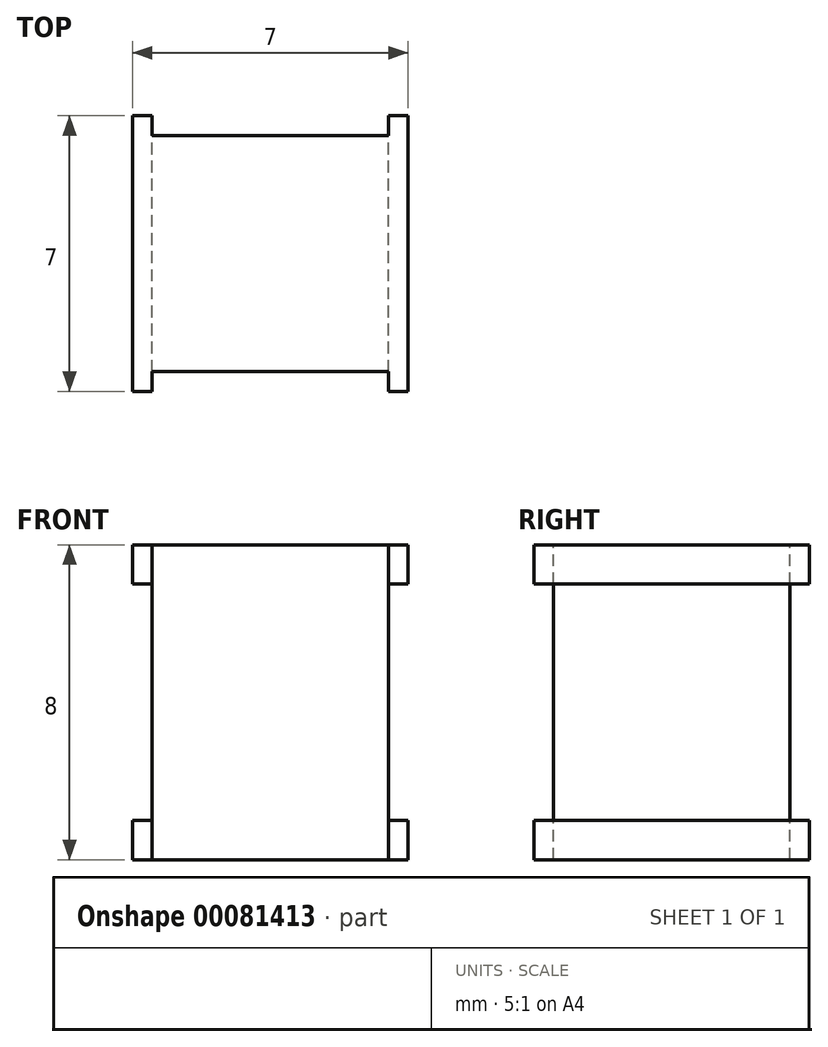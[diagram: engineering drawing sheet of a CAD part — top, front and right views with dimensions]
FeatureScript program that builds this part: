
annotation { "Feature Type Name" : "Feature", "Feature Type Description" : "" }
export const myFeature = defineFeature(function(context is Context, id is Id, definition is map)
    precondition{}
    {
        {
            var Q0;
            Q0=qCreatedBy(makeId("Top.planeOp"),FACE);
            var sketch = newSketch(context, id + "F0", { "sketchPlane" : qUnion([Q0])});
            skLineSegment(sketch, "E0.bottom", {"start": v(3, -3) * mm, "end": v(-3, -3) * mm});
            skLineSegment(sketch, "E0.top", {"start": v(3, 3) * mm, "end": v(-3, 3) * mm});
            skLineSegment(sketch, "E0.left", {"start": v(3, -3) * mm, "end": v(3, 3) * mm});
            skLineSegment(sketch, "E0.right", {"start": v(-3, -3) * mm, "end": v(-3, 3) * mm});
            skPoint(sketch, "E0.middle", {"position": v(0, 0) * mm});
            skSolve(sketch);
        }
        {
            var Q0;
            Q0=makeQuery(id+"F0.imprint","IMPRINT",FACE,{"disambiguationData":[TD([[makeQuery(id+"F0.imprint","IMPRINT",EDGE,{"derivedFrom":sQuery(id+"F0.wireOp",EDGE,"E0.bottom")}),-1.0]])]});
            extrude(context, id + "F1", {"entities" : qUnion([Q0]), "depth" : 6 * mm});
        }
        {
            var Q0;
            Q0=makeQuery(id+"F1.opExtrude","CAP_FACE",FACE,{"disambiguationData":[OSD([sQuery(id+"F0.wireOp",EDGE,"E0.bottom"),sQuery(id+"F0.wireOp",EDGE,"E0.top"),sQuery(id+"F0.wireOp",EDGE,"E0.left"),sQuery(id+"F0.wireOp",EDGE,"E0.right")])],"isStart":false});
            var sketch = newSketch(context, id + "F2", { "sketchPlane" : qUnion([Q0])});
            skLineSegment(sketch, "E1.bottom", {"start": v(3.5, -3.5) * mm, "end": v(-3.5, -3.5) * mm});
            skLineSegment(sketch, "E1.top", {"start": v(3.5, 3.5) * mm, "end": v(-3.5, 3.5) * mm});
            skLineSegment(sketch, "E1.left", {"start": v(3.5, -3.5) * mm, "end": v(3.5, 3.5) * mm});
            skLineSegment(sketch, "E1.right", {"start": v(-3.5, -3.5) * mm, "end": v(-3.5, 3.5) * mm});
            skPoint(sketch, "E1.middle", {"position": v(0, 0) * mm});
            skSolve(sketch);
        }
        {
            var Q0;
            Q0=qSketchRegion(id+"F2",true);
            extrude(context, id + "F3", {"entities" : qUnion([Q0]), "operationType" : NewBodyOperationType.ADD, "depth" : 1 * mm});
        }
        {
            var Q0;
            Q0=makeQuery(id+"F1.opExtrude","CAP_FACE",FACE,{"disambiguationData":[OSD([sQuery(id+"F0.wireOp",EDGE,"E0.bottom"),sQuery(id+"F0.wireOp",EDGE,"E0.top"),sQuery(id+"F0.wireOp",EDGE,"E0.left"),sQuery(id+"F0.wireOp",EDGE,"E0.right")])],"isStart":true});
            var sketch = newSketch(context, id + "F4", { "sketchPlane" : qUnion([Q0])});
            skLineSegment(sketch, "E2.0", {"start": v(3.5, -3.5) * mm, "end": v(-3.5, -3.5) * mm, "construction": true});
            skLineSegment(sketch, "E3.bottom", {"start": v(-3.5, -3.5) * mm, "end": v(3.5, -3.5) * mm, "construction": true});
            skLineSegment(sketch, "E3.top", {"start": v(-3.5, 3.5) * mm, "end": v(3.5, 3.5) * mm, "construction": true});
            skLineSegment(sketch, "E3.left", {"start": v(-3.5, -3.5) * mm, "end": v(-3.5, 3.5) * mm, "construction": true});
            skLineSegment(sketch, "E3.right", {"start": v(3.5, -3.5) * mm, "end": v(3.5, 3.5) * mm, "construction": true});
            skPoint(sketch, "E3.middle", {"position": v(0, 0) * mm});
            skLineSegment(sketch, "E4.bottom", {"start": v(-3.5, -3.5) * mm, "end": v(3.5, -3.5) * mm});
            skLineSegment(sketch, "E4.top", {"start": v(-3.5, 3.5) * mm, "end": v(3.5, 3.5) * mm});
            skLineSegment(sketch, "E4.left", {"start": v(-3.5, -3.5) * mm, "end": v(-3.5, 3.5) * mm});
            skLineSegment(sketch, "E4.right", {"start": v(3.5, -3.5) * mm, "end": v(3.5, 3.5) * mm});
            skSolve(sketch);
        }
        {
            var Q0;
            Q0=qSketchRegion(id+"F4",true);
            extrude(context, id + "F5", {"entities" : qUnion([Q0]), "operationType" : NewBodyOperationType.ADD, "depth" : 1 * mm});
        }
        {
            var Q0;
            Q0=makeQuery(id+"F3.opExtrude","CAP_FACE",FACE,{"disambiguationData":[OSD([sQuery(id+"F2.wireOp",EDGE,"E1.bottom"),sQuery(id+"F2.wireOp",EDGE,"E1.top"),sQuery(id+"F2.wireOp",EDGE,"E1.left"),sQuery(id+"F2.wireOp",EDGE,"E1.right")])],"isStart":false});
            var sketch = newSketch(context, id + "F6", { "sketchPlane" : qUnion([Q0])});
            skPoint(sketch, "E5.0", {"position": v(-3.5, 3.5) * mm});
            skLineSegment(sketch, "E6.0", {"start": v(3.5, 3.5) * mm, "end": v(-3.5, 3.5) * mm, "construction": true});
            skLineSegment(sketch, "E7.0", {"start": v(3.5, -3.5) * mm, "end": v(3.5, 3.5) * mm, "construction": true});
            skLineSegment(sketch, "E8.0", {"start": v(3.5, -3.5) * mm, "end": v(-3.5, -3.5) * mm, "construction": true});
            skLineSegment(sketch, "E9.0", {"start": v(3, -3) * mm, "end": v(-3, -3) * mm, "construction": true});
            skLineSegment(sketch, "E10.0", {"start": v(3, 3) * mm, "end": v(-3, 3) * mm, "construction": true});
            skLineSegment(sketch, "E11.bottom", {"start": v(3, 3) * mm, "end": v(-3, 3) * mm});
            skLineSegment(sketch, "E11.top", {"start": v(3, 3.5) * mm, "end": v(-3, 3.5) * mm});
            skLineSegment(sketch, "E11.left", {"start": v(3, 3) * mm, "end": v(3, 3.5) * mm});
            skLineSegment(sketch, "E11.right", {"start": v(-3, 3) * mm, "end": v(-3, 3.5) * mm});
            skLineSegment(sketch, "E12.bottom", {"start": v(3, -3) * mm, "end": v(-3, -3) * mm});
            skLineSegment(sketch, "E12.top", {"start": v(3, -3.5) * mm, "end": v(-3, -3.5) * mm});
            skLineSegment(sketch, "E12.left", {"start": v(3, -3) * mm, "end": v(3, -3.5) * mm});
            skLineSegment(sketch, "E12.right", {"start": v(-3, -3) * mm, "end": v(-3, -3.5) * mm});
            skSolve(sketch);
        }
        {
            var Q0;
            Q0 = qSketchRegion(id + "F6", true);
            extrude(context, id + "F7", {"entities" : qUnion([Q0]), "operationType" : NewBodyOperationType.REMOVE, "endBound" : BoundingType.THROUGH_ALL, "oppositeDirection" : true, "depth" : 25 * mm});
        }
    });
